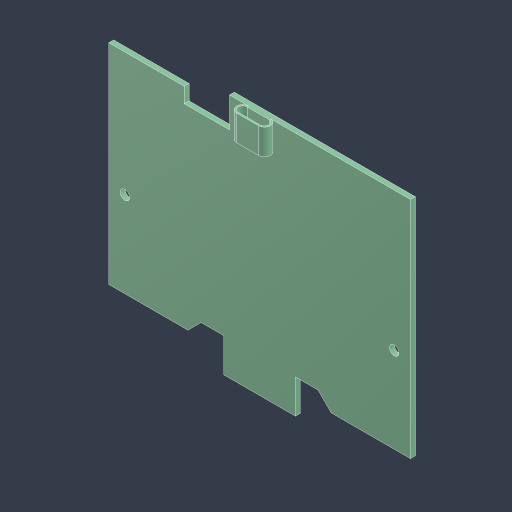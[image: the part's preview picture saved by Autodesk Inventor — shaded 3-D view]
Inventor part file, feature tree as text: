
AUTODESK INVENTOR PART (.ipt)
format: ipt  version: 2023.4 (Build 274418000, 418)  size: 146,944 bytes
history: native  units: mm
features: sketch x3, extrude x2, hole x1
ambient origin geometry x8: Origin, YZ Plane, XZ Plane, XY Plane, X Axis, Y Axis, Z Axis, Center Point
bodies: Solid1 (feature_tree)
feature tree (6):
  extrude  "Extrusion1"  Depth=65.0mm
  hole  "Hole1"  [1 undecoded]
  extrude  "Extrusion2"  Depth=3.5mm
  sketch  "Sketch1"  dims[d0=80.0mm d1=65.0mm]
  sketch  "Sketch2"  dims[d2=19.0mm d3=45.0deg]
  sketch  "Sketch4"  dims[d4=9.0mm d5=3.5mm d6=6.0mm d7=45.0deg d8=8.0mm d9=8.0mm d10=12.0mm d11=4.0mm d12=1.3mm d13=0.0mm d14=71.4mm d15=22.7mm d16=2.5mm d17=6.0mm d18=40.0mm d19=25.5mm d20=90.0deg d21=8.0mm d22=20.594885mm d23=3.2mm d24=9.0mm d25=0.4mm d26=6.8mm d27=0.0mm]
note: 1 required parameter value undecoded (feature->parameter linkage not recoverable at this tier; creation-order binding heuristic only, values carry confidence <= 0.55)
